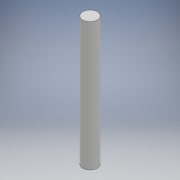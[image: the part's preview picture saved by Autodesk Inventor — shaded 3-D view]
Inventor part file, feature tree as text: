
AUTODESK INVENTOR PART (.ipt)
format: ipt  version: 2018 (Build 220112000, 112)  size: 89,088 bytes
history: native  units: mm
features: other x1, extrude x1, sketch x1
ambient origin geometry x8: Origin, YZ Plane, XZ Plane, XY Plane, X Axis, Y Axis, Z Axis, Center Point
bodies: Body1 (feature_tree)
feature tree (3):
  other  "ソリッド1"
  extrude  "押し出し1"  Depth=12.0mm
  sketch  "スケッチ1"
